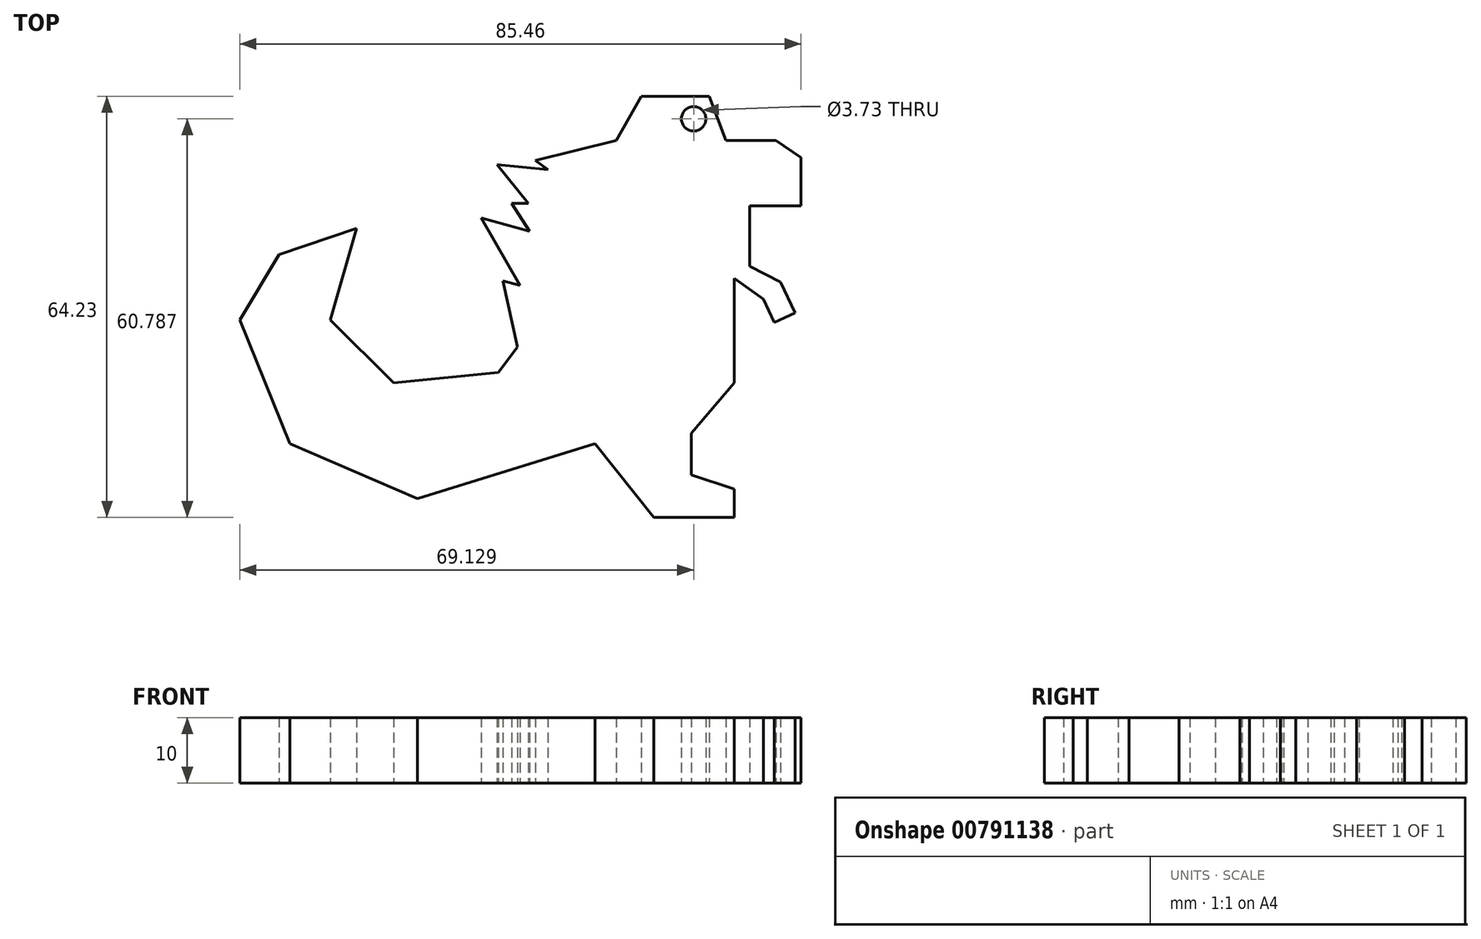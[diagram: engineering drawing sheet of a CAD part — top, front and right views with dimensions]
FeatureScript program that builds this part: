
annotation { "Feature Type Name" : "Feature", "Feature Type Description" : "" }
export const myFeature = defineFeature(function(context is Context, id is Id, definition is map)
    precondition{}
    {
        {
            var Q0;
            Q0=qCreatedBy(makeId("Top.planeOp"),FACE);
            var sketch = newSketch(context, id + "F0", { "sketchPlane" : qUnion([Q0])});
            skLineSegment(sketch, "E0", {"start": v(10.98, 38.74) * mm, "end": v(18.6, 38.74) * mm});
            skLineSegment(sketch, "E1", {"start": v(22.4, 28.76) * mm, "end": v(14.6, 28.76) * mm});
            skLineSegment(sketch, "E2", {"start": v(14.6, 28.76) * mm, "end": v(14.6, 19.5) * mm});
            skLineSegment(sketch, "E3", {"start": v(12.25, 17.7) * mm, "end": v(12.25, 1.72) * mm});
            skLineSegment(sketch, "E4", {"start": v(12.25, 1.72) * mm, "end": v(5.72, -5.9) * mm});
            skLineSegment(sketch, "E5", {"start": v(5.72, -5.9) * mm, "end": v(5.72, 6.26) * mm});
            skLineSegment(sketch, "E6", {"start": v(5.72, 6.26) * mm, "end": v(-4.08, 6.26) * mm});
            skLineSegment(sketch, "E7", {"start": v(-4.08, 6.26) * mm, "end": v(-8.98, -1.36) * mm});
            skLineSegment(sketch, "E8", {"start": v(-8.98, -1.36) * mm, "end": v(-8.98, -7.53) * mm});
            skLineSegment(sketch, "E9", {"start": v(-8.98, -7.53) * mm, "end": v(0, -18.78) * mm});
            skLineSegment(sketch, "E10", {"start": v(0, -18.78) * mm, "end": v(12.25, -18.78) * mm});
            skLineSegment(sketch, "E11", {"start": v(12.25, -18.78) * mm, "end": v(12.25, -14.43) * mm});
            skLineSegment(sketch, "E12", {"start": v(12.25, -14.43) * mm, "end": v(5.72, -12.25) * mm});
            skLineSegment(sketch, "E13", {"start": v(5.72, -12.25) * mm, "end": v(5.72, -5.9) * mm});
            skLineSegment(sketch, "E14", {"start": v(10.98, 38.74) * mm, "end": v(8.44, 45.45) * mm});
            skLineSegment(sketch, "E15", {"start": v(8.44, 45.45) * mm, "end": v(-1.9, 45.45) * mm});
            skLineSegment(sketch, "E16", {"start": v(-1.9, 45.45) * mm, "end": v(-5.72, 38.74) * mm});
            skLineSegment(sketch, "E17", {"start": v(-5.72, 38.74) * mm, "end": v(-11.52, 19.5) * mm});
            skLineSegment(sketch, "E18", {"start": v(-11.52, 19.5) * mm, "end": v(-23.68, 3.36) * mm});
            skLineSegment(sketch, "E19", {"start": v(-23.68, 3.36) * mm, "end": v(-39.65, 1.72) * mm});
            skLineSegment(sketch, "E20", {"start": v(-39.65, 1.72) * mm, "end": v(-49.26, 11.34) * mm});
            skLineSegment(sketch, "E21", {"start": v(-49.26, 11.34) * mm, "end": v(-45.27, 25.31) * mm});
            skLineSegment(sketch, "E22", {"start": v(-45.27, 25.31) * mm, "end": v(-57.07, 21.32) * mm});
            skLineSegment(sketch, "E23", {"start": v(-57.07, 21.32) * mm, "end": v(-63.05, 11.34) * mm});
            skLineSegment(sketch, "E24", {"start": v(-63.05, 11.34) * mm, "end": v(-55.43, -7.53) * mm});
            skLineSegment(sketch, "E25", {"start": v(-55.43, -7.53) * mm, "end": v(-36.02, -15.88) * mm});
            skLineSegment(sketch, "E26", {"start": v(-36.02, -15.88) * mm, "end": v(-8.98, -7.53) * mm});
            skLineSegment(sketch, "E27", {"start": v(22.4, 36.1) * mm, "end": v(22.4, 28.76) * mm});
            skLineSegment(sketch, "E28", {"start": v(14.6, 19.5) * mm, "end": v(19.32, 17.15) * mm});
            skLineSegment(sketch, "E29", {"start": v(19.32, 17.15) * mm, "end": v(21.5, 12.43) * mm});
            skLineSegment(sketch, "E30", {"start": v(21.5, 12.43) * mm, "end": v(18.35, 10.97) * mm});
            skLineSegment(sketch, "E31", {"start": v(18.35, 10.97) * mm, "end": v(16.7, 14.54) * mm});
            skLineSegment(sketch, "E32", {"start": v(16.7, 14.54) * mm, "end": v(12.25, 17.7) * mm});
            skCircle(sketch, "E33", {"center": v(6.08, 42) * mm, "radius": 1.86 * mm});
            skLineSegment(sketch, "E34", {"start": v(-5.72, 38.74) * mm, "end": v(-18.05, 35.66) * mm});
            skLineSegment(sketch, "E35", {"start": v(-18.05, 35.66) * mm, "end": v(-8.62, 29.12) * mm});
            skLineSegment(sketch, "E36", {"start": v(-8.62, 29.12) * mm, "end": v(-21.68, 29.12) * mm});
            skLineSegment(sketch, "E37", {"start": v(-21.68, 29.12) * mm, "end": v(-13.62, 16.72) * mm});
            skLineSegment(sketch, "E38", {"start": v(-13.62, 16.72) * mm, "end": v(-14.79, 17.33) * mm});
            skLineSegment(sketch, "E39", {"start": v(-14.86, 15.07) * mm, "end": v(-22.95, 17.33) * mm});
            skLineSegment(sketch, "E40", {"start": v(-22.95, 17.33) * mm, "end": v(-20.76, 7.24) * mm});
            skLineSegment(sketch, "E41", {"start": v(18.6, 38.74) * mm, "end": v(22.4, 36.1) * mm});
            skLineSegment(sketch, "E42", {"start": v(-23.9, 35.04) * mm, "end": v(-16.1, 34.3) * mm});
            skLineSegment(sketch, "E43", {"start": v(-18.9, 24.86) * mm, "end": v(-26.3, 26.92) * mm});
            skPoint(sketch, "E43.startSnap0", {"position": v(-18.9, 16.2) * mm});
            skLineSegment(sketch, "E44", {"start": v(-26.3, 26.92) * mm, "end": v(-20.35, 16.6) * mm});
            skLineSegment(sketch, "E45", {"start": v(-23.9, 35.04) * mm, "end": v(-19.1, 29.12) * mm});
            skLineSegment(sketch, "E46", {"start": v(-20.35, 16.6) * mm, "end": v(-18.9, 24.86) * mm});
            skLineSegment(sketch, "E47", {"start": v(-19.1, 29.12) * mm, "end": v(-16.1, 34.3) * mm});
            skSolve(sketch);
        }
        {
            var Q0;
            Q0=makeQuery(id+"F0.imprint","IMPRINT",FACE,{"disambiguationData":[TD([[makeQuery(id+"F0.imprint","IMPRINT",EDGE,{"derivedFrom":sQuery(id+"F0.wireOp",EDGE,"E0")}),-1.0]])]});
            extrude(context, id + "F1", {"entities" : qUnion([Q0]), "depth" : 9 * mm, "offsetDistance" : 25 * mm});
        }
        {
            var Q0;
            Q0 = qSketchRegion(id + "F0", true);
            extrude(context, id + "F2", {"entities" : qUnion([Q0]), "operationType" : NewBodyOperationType.ADD, "depth" : 10 * mm, "offsetDistance" : 25 * mm});
        }
        {
            var Q0;
            Q0=makeQuery(id+"F2.opExtrude","CAP_FACE",FACE,{"disambiguationData":[OSD([sQuery(id+"F0.wireOp",EDGE,"E0"),sQuery(id+"F0.wireOp",EDGE,"E1"),sQuery(id+"F0.wireOp",EDGE,"E2"),sQuery(id+"F0.wireOp",EDGE,"E3"),sQuery(id+"F0.wireOp",EDGE,"E4"),sQuery(id+"F0.wireOp",EDGE,"E9"),sQuery(id+"F0.wireOp",EDGE,"E10"),sQuery(id+"F0.wireOp",EDGE,"E11"),sQuery(id+"F0.wireOp",EDGE,"E12"),sQuery(id+"F0.wireOp",EDGE,"E13"),sQuery(id+"F0.wireOp",EDGE,"E14"),sQuery(id+"F0.wireOp",EDGE,"E15"),sQuery(id+"F0.wireOp",EDGE,"E16"),sQuery(id+"F0.wireOp",EDGE,"E18"),sQuery(id+"F0.wireOp",EDGE,"E19"),sQuery(id+"F0.wireOp",EDGE,"E20"),sQuery(id+"F0.wireOp",EDGE,"E21"),sQuery(id+"F0.wireOp",EDGE,"E22"),sQuery(id+"F0.wireOp",EDGE,"E23"),sQuery(id+"F0.wireOp",EDGE,"E24"),sQuery(id+"F0.wireOp",EDGE,"E25"),sQuery(id+"F0.wireOp",EDGE,"E26"),sQuery(id+"F0.wireOp",EDGE,"E27"),sQuery(id+"F0.wireOp",EDGE,"E28"),sQuery(id+"F0.wireOp",EDGE,"E29"),sQuery(id+"F0.wireOp",EDGE,"E30"),sQuery(id+"F0.wireOp",EDGE,"E31"),sQuery(id+"F0.wireOp",EDGE,"E32"),sQuery(id+"F0.wireOp",EDGE,"E33"),sQuery(id+"F0.wireOp",EDGE,"E34"),sQuery(id+"F0.wireOp",EDGE,"E35"),sQuery(id+"F0.wireOp",EDGE,"E36"),sQuery(id+"F0.wireOp",EDGE,"E37"),sQuery(id+"F0.wireOp",EDGE,"E39"),sQuery(id+"F0.wireOp",EDGE,"E40"),sQuery(id+"F0.wireOp",EDGE,"E41"),sQuery(id+"F0.wireOp",EDGE,"E42"),sQuery(id+"F0.wireOp",EDGE,"E43"),sQuery(id+"F0.wireOp",EDGE,"E44"),sQuery(id+"F0.wireOp",EDGE,"E45")])],"isStart":false});
            extrude(context, id + "F3", {"entities" : qUnion([Q0]), "operationType" : NewBodyOperationType.ADD, "oppositeDirection" : true, "depth" : 1.1 * mm, "offsetDistance" : 25 * mm});
        }
    });
